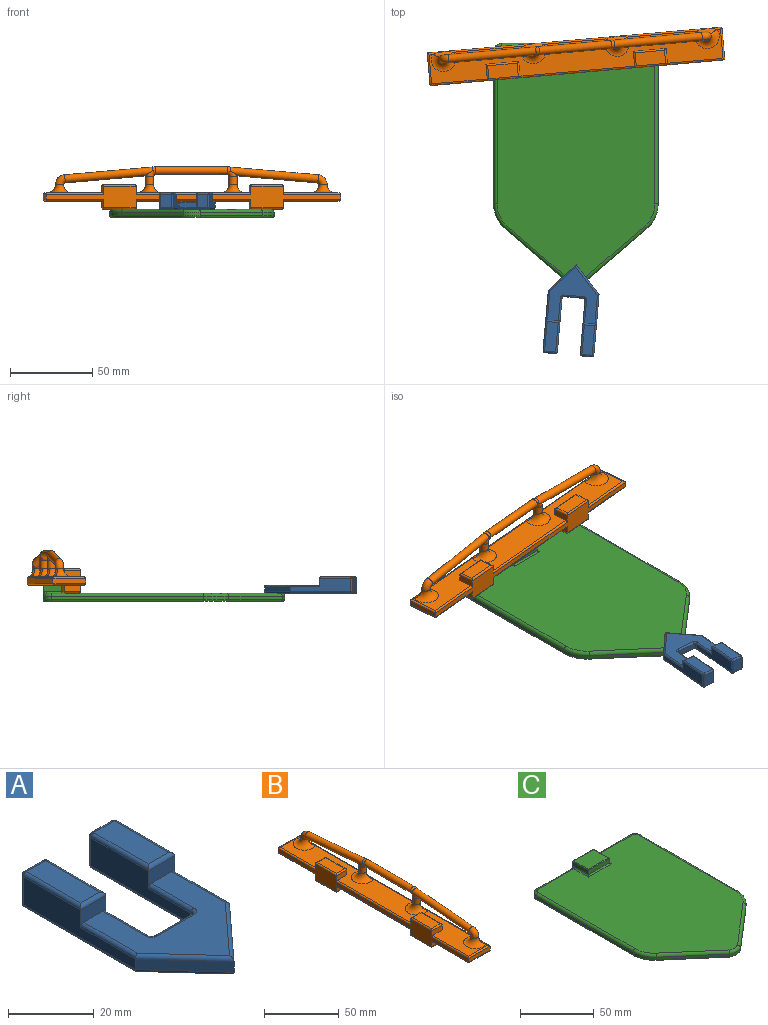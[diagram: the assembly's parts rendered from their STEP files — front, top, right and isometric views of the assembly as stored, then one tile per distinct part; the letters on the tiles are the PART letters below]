
ASSEMBLY  parts=3 mates=2
PART A: 57 faces, bbox 31x55x10 mm
  f0: plane 17x15.5mm, normal (-0.74,-0.67,0), area 69mm2, adj f1,f6,f22,f26
  f1: plane 17x15.5mm, normal (0.74,-0.67,0), area 69mm2, adj f0,f2,f23,f27
  f2: plane 37x8mm, normal (1,0,0), area 206mm2, adj f1,f24,f28,f43,f51,f56
  f3: plane 33x8mm, normal (-1,0,0), area 194mm2, adj f9,f13,f14,f43,f46,f47
  f4: plane 12x3mm, normal (0,1,0), area 36mm2, adj f12,f13,f17,f18
  f5: plane 33x8mm, normal (1,0,0), area 194mm2, adj f11,f17,f20,f29,f32,f33
  f6: plane 37x8mm, normal (-1,0,0), area 206mm2, adj f0,f21,f25,f29,f38,f42
  f7: plane 33.52x29mm, normal (0,0,1), area 487.1mm2, adj f14,f16,f18,f19,f20,f25,f26,f27
  f8: plane 52.52x29mm, normal (0,0,-1), area 734.1mm2, adj f9,f10,f11,f12,f15,f21,f22,f23
  f9: cylinder r=1mm len=33mm, axis (0,-1,0), area 51.8mm2, adj f3,f8,f10,f50
  f10: torus R=2mm, axis (0,0,1), area 3.4mm2, adj f8,f9,f12,f13
  f11: cylinder r=1mm len=33mm, axis (0,1,0), area 51.8mm2, adj f5,f8,f15,f36
  f12: cylinder r=1mm len=12mm, axis (-1,0,0), area 18.8mm2, adj f4,f8,f10,f15
  f13: cylinder r=1mm len=3mm, axis (0,0,1), area 4.7mm2, adj f3,f4,f10,f16
  f14: cylinder r=1mm len=14mm, axis (0,1,0), area 22mm2, adj f3,f7,f16,f43
  f15: torus R=2mm, axis (0,0,1), area 3.4mm2, adj f8,f11,f12,f17
  f16: torus R=2mm, axis (0,0,1), area 3.4mm2, adj f7,f13,f14,f18
  f17: cylinder r=1mm len=3mm, axis (0,0,-1), area 4.7mm2, adj f4,f5,f15,f19
  f18: cylinder r=1mm len=12mm, axis (1,0,0), area 18.8mm2, adj f4,f7,f16,f19
  f19: torus R=2mm, axis (0,0,1), area 3.4mm2, adj f7,f17,f18,f20
  f20: cylinder r=1mm len=14mm, axis (0,-1,0), area 22mm2, adj f5,f7,f19,f29
  f21: cylinder r=1mm len=37mm, axis (0,-1,0), area 57.9mm2, adj f6,f8,f22,f41
  f22: cylinder r=1mm len=17.67mm, axis (0.67,-0.74,0), area 35.3mm2, adj f0,f8,f21,f23
  f23: cylinder r=1mm len=17.67mm, axis (0.67,0.74,0), area 35.3mm2, adj f1,f8,f22,f24
  f24: cylinder r=1mm len=37mm, axis (0,1,0), area 57.9mm2, adj f2,f8,f23,f55
  f25: cylinder r=1mm len=18mm, axis (0,1,0), area 28.1mm2, adj f6,f7,f26,f29
  f26: cylinder r=1mm len=17.67mm, axis (-0.67,0.74,0), area 35.3mm2, adj f0,f7,f25,f27
  f27: cylinder r=1mm len=17.67mm, axis (-0.67,-0.74,0), area 35.3mm2, adj f1,f7,f26,f28
  f28: cylinder r=1mm len=18mm, axis (0,-1,0), area 28.1mm2, adj f2,f7,f27,f43
  f29: plane 8.28x5mm, normal (0,-1,0), area 33.5mm2, adj f5,f6,f7,f20,f25,f35
  f30: plane 8x6.28mm, normal (0,1,0), area 50.2mm2, adj f33,f37,f39,f42
  f31: plane 18x6.28mm, normal (0,0,1), area 113mm2, adj f32,f35,f37,f38
  f32: cylinder r=1mm len=19mm, axis (0,-1,0), area 29.3mm2, adj f5,f31,f34,f35
  f33: cylinder r=1mm len=8mm, axis (0,0,1), area 12.6mm2, adj f5,f30,f34,f36
  f34: sphere r=1mm, area 1.6mm2, adj f32,f33,f37
  f35: cylinder r=1mm len=8.28mm, axis (-1,0,0), area 11.9mm2, adj f29,f31,f32,f38
  f36: sphere r=1mm, area 1.6mm2, adj f11,f33,f39
  f37: cylinder r=1mm len=6.28mm, axis (1,0,0), area 9.9mm2, adj f30,f31,f34,f40
  f38: cylinder r=1mm len=19mm, axis (0,1,0), area 29.3mm2, adj f6,f31,f35,f40
  f39: cylinder r=1mm len=6.28mm, axis (-1,0,0), area 9.9mm2, adj f8,f30,f36,f41
  f40: sphere r=1mm, area 1.6mm2, adj f37,f38,f42
  f41: sphere r=1mm, area 1.6mm2, adj f21,f39,f42
  f42: cylinder r=1mm len=8mm, axis (0,0,1), area 12.6mm2, adj f6,f30,f40,f41
  f43: plane 8.72x5mm, normal (0,-1,0), area 35.3mm2, adj f2,f3,f7,f14,f28,f48
  f44: plane 8x6.72mm, normal (0,1,0), area 53.8mm2, adj f47,f52,f53,f56
  f45: plane 18x6.72mm, normal (0,0,1), area 121mm2, adj f46,f48,f51,f52
  f46: cylinder r=1mm len=19mm, axis (0,1,0), area 29.3mm2, adj f3,f45,f48,f49
  f47: cylinder r=1mm len=8mm, axis (0,0,-1), area 12.6mm2, adj f3,f44,f49,f50
  f48: cylinder r=1mm len=8.72mm, axis (-1,0,0), area 12.6mm2, adj f43,f45,f46,f51
  f49: sphere r=1mm, area 1.6mm2, adj f46,f47,f52
  f50: sphere r=1mm, area 1.6mm2, adj f9,f47,f53
  f51: cylinder r=1mm len=19mm, axis (0,-1,0), area 29.3mm2, adj f2,f45,f48,f54
  f52: cylinder r=1mm len=6.72mm, axis (1,0,0), area 10.6mm2, adj f44,f45,f49,f54
  f53: cylinder r=1mm len=6.72mm, axis (-1,0,0), area 10.6mm2, adj f8,f44,f50,f55
  f54: sphere r=1mm, area 1.6mm2, adj f51,f52,f56
  f55: sphere r=1mm, area 1.6mm2, adj f24,f53,f56
  f56: cylinder r=1mm len=8mm, axis (0,0,-1), area 12.6mm2, adj f2,f44,f54,f55
PART B: 69 faces, bbox 21.2x184.9x26.5 mm
  f0: cylinder r=2.5mm len=44mm, axis (0,1,0), area 691.2mm2, adj f40,f68
  f1: plane 10x5mm, normal (0,1,0), area 40.2mm2, adj f5,f7,f15,f23,f35
  f2: plane 10x5mm, normal (0,1,0), area 40.2mm2, adj f4,f5,f11,f24,f29
  f3: plane 10x5mm, normal (0,-1,0), area 40.2mm2, adj f5,f7,f16,f23,f36
  f4: plane 20x4mm, normal (1,0,0), area 80mm2, adj f2,f6,f10,f24
  f5: plane 180x13mm, normal (-1,0,0), area 940mm2, adj f1,f2,f3,f6,f13,f17,f20,f22
  f6: plane 10x5mm, normal (0,-1,0), area 40.2mm2, adj f4,f5,f12,f24,f30
  f7: plane 20x4mm, normal (1,0,0), area 80mm2, adj f1,f3,f14,f23
  f8: plane 18x8mm, normal (0,0,1), area 144mm2, adj f14,f15,f16,f17
  f9: plane 18x8mm, normal (0,0,-1), area 144mm2, adj f10,f11,f12,f13
  f10: cylinder r=1mm len=20mm, axis (0,1,0), area 30.3mm2, adj f4,f9,f11,f12
  f11: cylinder r=1mm len=10mm, axis (-1,0,0), area 14.6mm2, adj f2,f9,f10,f13
  f12: cylinder r=1mm len=10mm, axis (1,0,0), area 14.6mm2, adj f6,f9,f10,f13
  f13: cylinder r=1mm len=20mm, axis (0,-1,0), area 30.3mm2, adj f5,f9,f11,f12
  f14: cylinder r=1mm len=20mm, axis (0,-1,0), area 30.3mm2, adj f7,f8,f15,f16
  f15: cylinder r=1mm len=10mm, axis (1,0,0), area 14.6mm2, adj f1,f8,f14,f17
  f16: cylinder r=1mm len=10mm, axis (-1,0,0), area 14.6mm2, adj f3,f8,f14,f17
  f17: cylinder r=1mm len=20mm, axis (0,1,0), area 30.3mm2, adj f5,f8,f15,f16
  f18: cylinder r=2.5mm len=4.36mm, axis (0,0,-1), area 3.7mm2, adj f39,f47
  f19: cylinder r=2.5mm len=4.36mm, axis (0,0,-1), area 3.7mm2, adj f42,f45
  f20: plane 20x3mm, normal (0,-1,0), area 60mm2, adj f5,f21,f26,f32
  f21: plane 180x3mm, normal (1,0,0), area 540mm2, adj f20,f22,f27,f33
  f22: plane 20x3mm, normal (0,1,0), area 60mm2, adj f5,f21,f28,f34
  f23: plane 178x18mm, normal (0,0,1), area 2279mm2, adj f1,f3,f7,f31,f32,f33,f34,f35
  f24: plane 178x18mm, normal (0,0,-1), area 2844mm2, adj f2,f4,f6,f25,f26,f27,f28,f29
  f25: cylinder r=1mm len=35mm, axis (0,-1,0), area 54.4mm2, adj f5,f24,f26,f54
  f26: cylinder r=1mm len=20mm, axis (1,0,0), area 30.3mm2, adj f20,f24,f25,f27
  f27: cylinder r=1mm len=180mm, axis (0,1,0), area 281.6mm2, adj f21,f24,f26,f28
  f28: cylinder r=1mm len=20mm, axis (-1,0,0), area 30.3mm2, adj f22,f24,f27,f29
  f29: cylinder r=1mm len=35mm, axis (0,-1,0), area 54.4mm2, adj f2,f5,f24,f28
  f30: cylinder r=1mm len=70mm, axis (0,-1,0), area 110mm2, adj f5,f6,f24,f56
  f31: cylinder r=1mm len=35mm, axis (0,1,0), area 54.4mm2, adj f5,f23,f32,f53
  f32: cylinder r=1mm len=20mm, axis (-1,0,0), area 30.3mm2, adj f20,f23,f31,f33
  f33: cylinder r=1mm len=180mm, axis (0,-1,0), area 256.6mm2, adj f21,f23,f32,f34,f45,f47,f49,f51
  f34: cylinder r=1mm len=20mm, axis (1,0,0), area 30.3mm2, adj f22,f23,f33,f35
  f35: cylinder r=1mm len=35mm, axis (0,1,0), area 54.4mm2, adj f1,f5,f23,f34
  f36: cylinder r=1mm len=70mm, axis (0,1,0), area 110mm2, adj f3,f5,f23,f55
  f37: cylinder r=2.5mm len=6.38mm, axis (0,0,-1), area 82.2mm2, adj f50,f51,f68
  f38: cylinder r=2.5mm len=6.38mm, axis (0,0,-1), area 82.2mm2, adj f40,f48,f49
  f39: torus R=3.5mm, axis (1,0,0), area 81.6mm2, adj f18,f41,f46
  f40: torus R=3.5mm, axis (1,0,0), area 48.8mm2, adj f0,f38,f41
  f41: cylinder r=2.5mm len=54.33mm, axis (0,-1,-0.09), area 820.5mm2, adj f39,f40
  f42: torus R=3.5mm, axis (-1,0,0), area 81.6mm2, adj f19,f43,f44
  f43: cylinder r=2.5mm len=54.33mm, axis (0,1,-0.09), area 820.5mm2, adj f42,f68
  f44: torus R=7.5mm, axis (0,0,1), area 141.3mm2, adj f23,f42,f45
  f45: bspline ~13.66x5.23mm, area 42.3mm2, adj f19,f33,f44
  f46: torus R=7.5mm, axis (0,0,1), area 141.3mm2, adj f23,f39,f47
  f47: bspline ~13.66x5.23mm, area 42.3mm2, adj f18,f33,f46
  f48: torus R=7.5mm, axis (0,0,1), area 141.3mm2, adj f23,f38,f49
  f49: bspline ~13.66x5.23mm, area 42.3mm2, adj f33,f38,f48
  f50: torus R=7.5mm, axis (0,0,1), area 141.3mm2, adj f23,f37,f51
  f51: bspline ~13.66x5.23mm, area 42.3mm2, adj f33,f37,f50
  f52: plane 20x4mm, normal (1,0,0), area 80mm2, adj f24,f54,f56,f62
  f53: plane 10x5mm, normal (0,-1,0), area 40.2mm2, adj f5,f23,f31,f57,f67
  f54: plane 10x5mm, normal (0,-1,0), area 40.2mm2, adj f5,f24,f25,f52,f63
  f55: plane 10x5mm, normal (0,1,0), area 40.2mm2, adj f5,f23,f36,f57,f64
  f56: plane 10x5mm, normal (0,1,0), area 40.2mm2, adj f5,f24,f30,f52,f60
  f57: plane 20x4mm, normal (1,0,0), area 80mm2, adj f23,f53,f55,f66
  f58: plane 18x8mm, normal (0,0,1), area 144mm2, adj f64,f65,f66,f67
  f59: plane 18x8mm, normal (0,0,-1), area 144mm2, adj f60,f61,f62,f63
  f60: cylinder r=1mm len=10mm, axis (-1,0,0), area 14.6mm2, adj f56,f59,f61,f62
  f61: cylinder r=1mm len=20mm, axis (0,-1,0), area 30.3mm2, adj f5,f59,f60,f63
  f62: cylinder r=1mm len=20mm, axis (0,1,0), area 30.3mm2, adj f52,f59,f60,f63
  f63: cylinder r=1mm len=10mm, axis (1,0,0), area 14.6mm2, adj f54,f59,f61,f62
  f64: cylinder r=1mm len=10mm, axis (1,0,0), area 14.6mm2, adj f55,f58,f65,f66
  f65: cylinder r=1mm len=20mm, axis (0,1,0), area 30.3mm2, adj f5,f58,f64,f67
  f66: cylinder r=1mm len=20mm, axis (0,-1,0), area 30.3mm2, adj f57,f58,f64,f67
  f67: cylinder r=1mm len=10mm, axis (-1,0,0), area 14.6mm2, adj f53,f58,f65,f66
  f68: torus R=3.5mm, axis (-1,0,0), area 48.8mm2, adj f0,f37,f43
PART C: 46 faces, bbox 103.3x149.8x10 mm
  f0: plane 142.89x96mm, normal (0,0,1), area 11636mm2, adj f1,f13,f14,f15,f16,f17,f18,f19
  f1: cylinder r=2mm len=34mm, axis (1,0,0), area 106.8mm2, adj f0,f4,f22,f41
  f2: plane 37.82x32.5mm, normal (0.65,-0.76,0), area 99.7mm2, adj f8,f10,f13,f23
  f3: plane 144.89x98mm, normal (0,0,-1), area 12371.1mm2, adj f23,f24,f25,f26,f27,f28,f29,f30
  f4: plane 90x8.5mm, normal (0,1,0), area 311.6mm2, adj f1,f11,f12,f20,f31,f33,f34,f37
  f5: plane 92.85x2mm, normal (-1,0,0), area 185.7mm2, adj f9,f11,f21,f30
  f6: plane 37.82x32.5mm, normal (-0.65,-0.76,0), area 99.7mm2, adj f8,f9,f17,f26
  f7: plane 92.85x2mm, normal (1,0,0), area 185.7mm2, adj f10,f12,f16,f27
  f8: cylinder r=10.6mm len=10.42mm, axis (0,0,1), area 21.8mm2, adj f2,f6,f15,f24
  f9: cylinder r=20mm len=15.17mm, axis (0,0,1), area 34.4mm2, adj f5,f6,f19,f28
  f10: cylinder r=20mm len=15.17mm, axis (0,0,-1), area 34.4mm2, adj f2,f7,f14,f25
  f11: cylinder r=5mm len=5mm, axis (0,0,-1), area 15.7mm2, adj f4,f5,f22,f32
  f12: cylinder r=5mm len=5mm, axis (0,0,1), area 15.7mm2, adj f4,f7,f18,f29
  f13: cylinder r=2mm len=39.13mm, axis (-0.76,-0.65,0), area 156.4mm2, adj f0,f2,f14,f15
  f14: torus R=18mm, axis (0,0,1), area 52.1mm2, adj f0,f10,f13,f16
  f15: torus R=8.6mm, axis (0,0,1), area 31.4mm2, adj f0,f8,f13,f17
  f16: cylinder r=2mm len=92.85mm, axis (0,-1,0), area 291.7mm2, adj f0,f7,f14,f18
  f17: cylinder r=2mm len=39.13mm, axis (-0.76,0.65,0), area 156.4mm2, adj f0,f6,f15,f19
  f18: torus R=3mm, axis (0,0,1), area 21.1mm2, adj f0,f12,f16,f20
  f19: torus R=18mm, axis (0,0,1), area 52.1mm2, adj f0,f9,f17,f21
  f20: cylinder r=2mm len=34mm, axis (1,0,0), area 106.8mm2, adj f0,f4,f18,f37
  f21: cylinder r=2mm len=92.85mm, axis (0,1,0), area 291.7mm2, adj f0,f5,f19,f22
  f22: torus R=3mm, axis (0,0,1), area 21.1mm2, adj f0,f1,f11,f21
  f23: cylinder r=1mm len=38.47mm, axis (0.76,0.65,0), area 78.3mm2, adj f2,f3,f24,f25
  f24: torus R=9.6mm, axis (0,0,1), area 16.4mm2, adj f3,f8,f23,f26
  f25: torus R=19mm, axis (0,0,1), area 26.6mm2, adj f3,f10,f23,f27
  f26: cylinder r=1mm len=38.47mm, axis (0.76,-0.65,0), area 78.3mm2, adj f3,f6,f24,f28
  f27: cylinder r=1mm len=92.85mm, axis (0,1,0), area 145.9mm2, adj f3,f7,f25,f29
  f28: torus R=19mm, axis (0,0,1), area 26.6mm2, adj f3,f9,f26,f30
  f29: torus R=4mm, axis (0,0,1), area 11.4mm2, adj f3,f12,f27,f31
  f30: cylinder r=1mm len=92.85mm, axis (0,-1,0), area 145.9mm2, adj f3,f5,f28,f32
  f31: cylinder r=1mm len=90mm, axis (-1,0,0), area 141.4mm2, adj f3,f4,f29,f32
  f32: torus R=4mm, axis (0,0,1), area 11.4mm2, adj f3,f11,f30,f31
  f33: plane 15x4.26mm, normal (-1,0,0), area 53mm2, adj f4,f35,f40,f41,f44
  f34: plane 15x4.26mm, normal (1,0,0), area 53mm2, adj f4,f35,f37,f38,f43
  f35: plane 20x3.5mm, normal (0,-1,0), area 70mm2, adj f33,f34,f39,f45
  f36: plane 19x14mm, normal (0,0,1), area 266mm2, adj f42,f43,f44,f45
  f37: torus R=3mm, axis (1,0,0), area 3.9mm2, adj f4,f20,f34,f38
  f38: cylinder r=1mm len=14mm, axis (0,-1,0), area 21mm2, adj f0,f34,f37,f39
  f39: cylinder r=1mm len=22mm, axis (-1,0,0), area 32.6mm2, adj f0,f35,f38,f40
  f40: cylinder r=1mm len=14mm, axis (0,1,0), area 21mm2, adj f0,f33,f39,f41
  f41: torus R=3mm, axis (1,0,0), area 3.9mm2, adj f1,f4,f33,f40
  f42: cylinder r=0.5mm len=20mm, axis (1,0,0), area 15.4mm2, adj f4,f36,f43,f44
  f43: cylinder r=0.5mm len=15mm, axis (0,-1,0), area 11.5mm2, adj f34,f36,f42,f45
  f44: cylinder r=0.5mm len=15mm, axis (0,1,0), area 11.5mm2, adj f33,f36,f42,f45
  f45: cylinder r=0.5mm len=20mm, axis (-1,0,0), area 15.4mm2, adj f35,f36,f43,f44
PLACE A rot(axis=(0,0,1),175deg) t=(218.31,-4.91,12.35)mm
PLACE B rot(axis=(0,0,1),95deg) t=(118.14,247.46,19.85)mm
PLACE C t=(132.5,95.45,7.35)mm
MATE revolute C.f8 <-> A.f8  axis (0,0,1) through (132.5,12.68,12.35)mm
MATE revolute B.f24 <-> C.f36  axis (0,0,-1) through (132.5,141.46,17.35)mm
